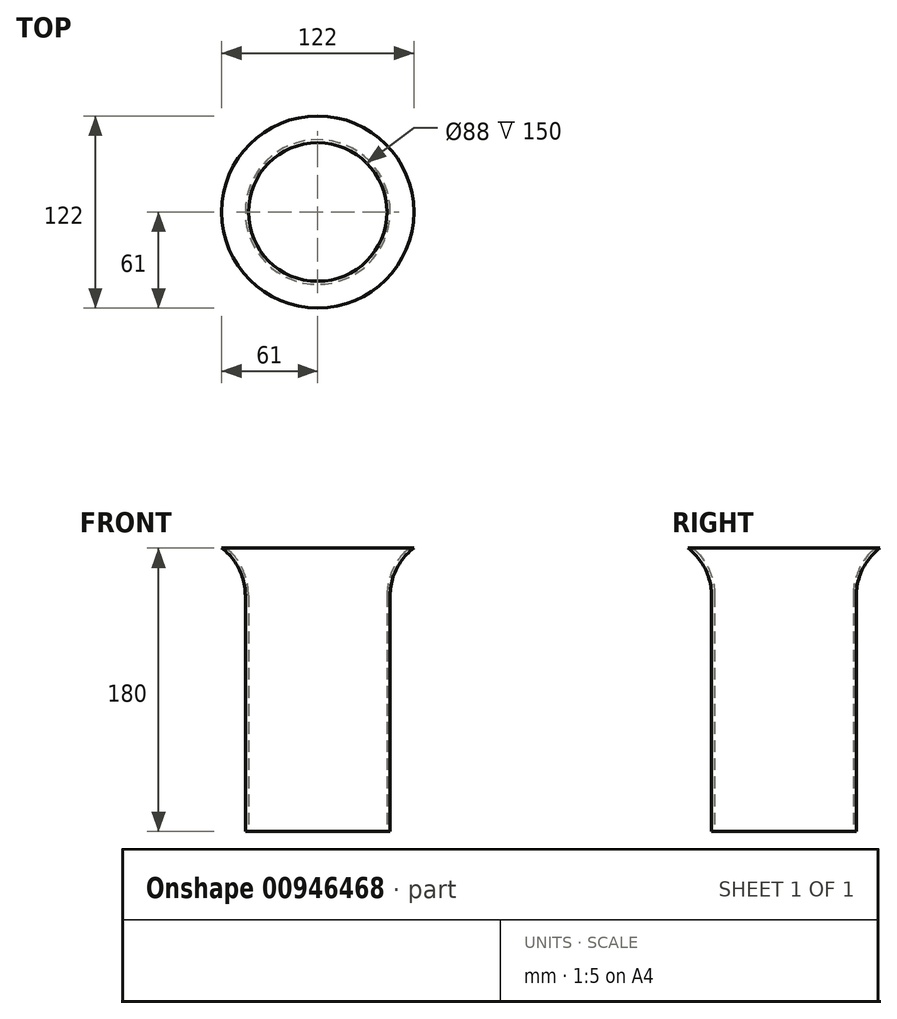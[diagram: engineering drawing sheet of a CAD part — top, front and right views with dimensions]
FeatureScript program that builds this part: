
annotation { "Feature Type Name" : "Feature", "Feature Type Description" : "" }
export const myFeature = defineFeature(function(context is Context, id is Id, definition is map)
    precondition{}
    {
        {
            var Q0;
            Q0=qCreatedBy(makeId("Front.planeOp"),FACE);
            var sketch = newSketch(context, id + "F0", { "sketchPlane" : qUnion([Q0])});
            skLineSegment(sketch, "E0", {"start": v(0, 0) * mm, "end": v(46, 0) * mm});
            skLineSegment(sketch, "E1", {"start": v(46, 0) * mm, "end": v(46, 150) * mm});
            skLineSegment(sketch, "E2", {"start": v(0, 0) * mm, "end": v(0, 180) * mm});
            skLineSegment(sketch, "E3", {"start": v(0, 180) * mm, "end": v(61, 180) * mm});
            skArc(sketch, "E4", {"start": v(46, 150) * mm, "mid": v(49.96, 166.77) * mm, "end": v(61, 180) * mm});
            skSolve(sketch);
        }
        {
            var Q0;
            Q0=makeQuery(id+"F0.imprint","IMPRINT",FACE,{"disambiguationData":[TD([[makeQuery(id+"F0.imprint","IMPRINT",EDGE,{"derivedFrom":sQuery(id+"F0.wireOp",EDGE,"E0")}),1.0]])]});
            var Q1;
            Q1=sQuery(id+"F0.wireOp",EDGE,"E2");
            revolve(context, id + "F1", {"surfaceOperationType" : NewSurfaceOperationType.NEW, "entities" : qUnion([Q0]), "axis" : qUnion([Q1]), "revolveType" : RevolveType.FULL});
        }
        {
            var Q0;
            Q0=makeQuery(id+"F1.opRevolve","SWEPT_FACE",FACE,{"disambiguationData":[OSD([sQuery(id+"F0.wireOp",EDGE,"E3")])]});
            var Q1;
            Q1=makeQuery(id+"F1.opRevolve","SWEPT_FACE",FACE,{"disambiguationData":[OSD([sQuery(id+"F0.wireOp",EDGE,"E0")])]});
            shell(context, id + "F2", {"entities" : qUnion([Q0, Q1]), "thickness" : 2 * mm});
        }
        {
            var Q0;
            Q0=makeQuery(id+"F2.opShell","OFFSET_EDGE",EDGE,{"disambiguationData":[OSD([sQuery(id+"F0.wireOp",EDGE,"E3"),sQuery(id+"F0.wireOp",EDGE,"2e58bf21-b871-4623-80a6-0a6824290bb7")])]});
            fillet(context, id + "F3", {"entities" : qUnion([Q0]), "radius" : 8 * mm, "tangentPropagation" : true, "allowEdgeOverflow" : false});
        }
    });
